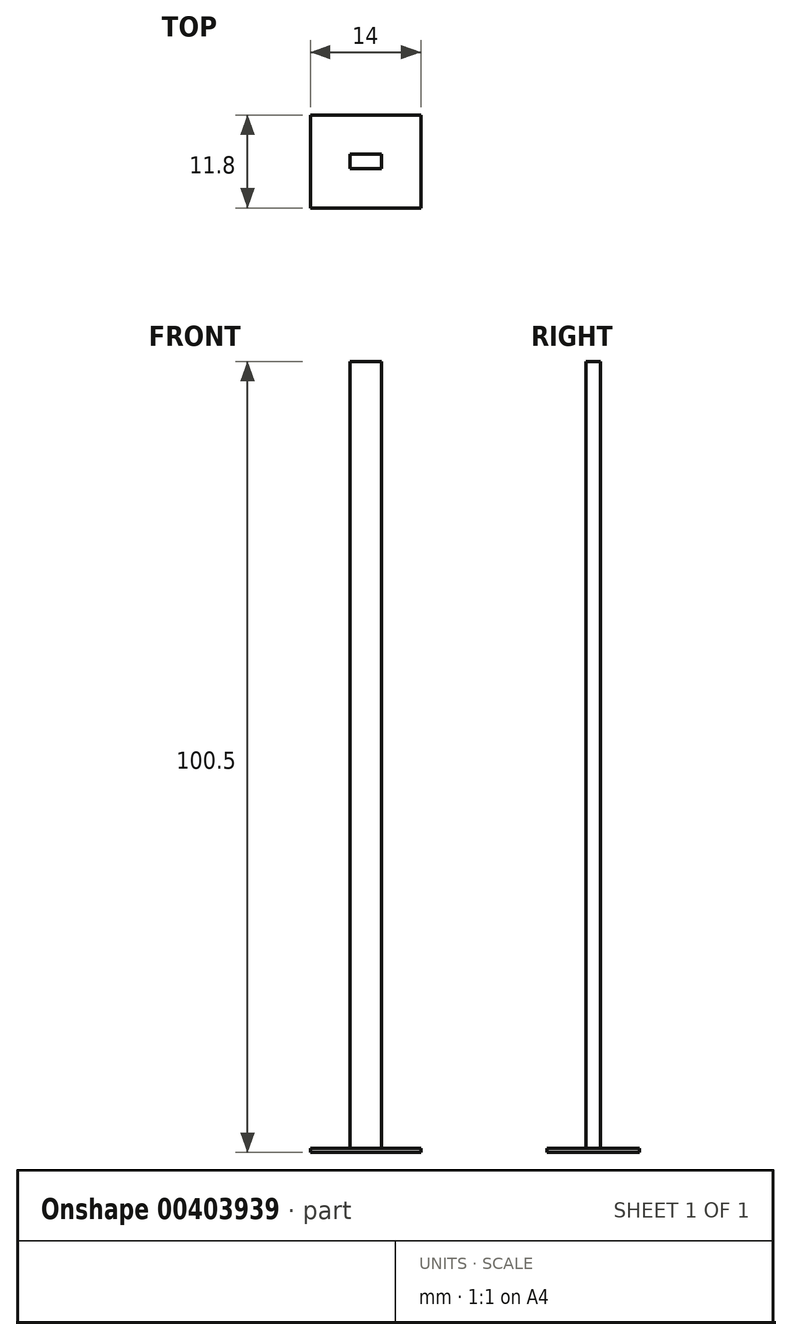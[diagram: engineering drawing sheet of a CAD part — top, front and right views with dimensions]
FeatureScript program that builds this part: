
annotation { "Feature Type Name" : "Feature", "Feature Type Description" : "" }
export const myFeature = defineFeature(function(context is Context, id is Id, definition is map)
    precondition{}
    {
        {
            var Q0;
            Q0=qCreatedBy(makeId("Top.planeOp"),FACE);
            var sketch = newSketch(context, id + "F0", { "sketchPlane" : qUnion([Q0])});
            skLineSegment(sketch, "E0.bottom", {"start": v(0, 0) * mm, "end": v(4, 0) * mm});
            skLineSegment(sketch, "E0.top", {"start": v(0, -1.8) * mm, "end": v(4, -1.8) * mm});
            skLineSegment(sketch, "E0.left", {"start": v(0, 0) * mm, "end": v(0, -1.8) * mm});
            skLineSegment(sketch, "E0.right", {"start": v(4, 0) * mm, "end": v(4, -1.8) * mm});
            skLineSegment(sketch, "E1.0", {"start": v(-5, 5) * mm, "end": v(9, 5) * mm});
            skLineSegment(sketch, "E1.1", {"start": v(-5, 5) * mm, "end": v(-5, -6.8) * mm});
            skLineSegment(sketch, "E1.2", {"start": v(-5, -6.8) * mm, "end": v(9, -6.8) * mm});
            skLineSegment(sketch, "E1.3", {"start": v(9, 5) * mm, "end": v(9, -6.8) * mm});
            skSolve(sketch);
        }
        {
            var Q0;
            Q0=makeQuery(id+"F0.imprint","IMPRINT",FACE,{"disambiguationData":[TD([[makeQuery(id+"F0.imprint","IMPRINT",EDGE,{"derivedFrom":sQuery(id+"F0.wireOp",EDGE,"E0.bottom")}),-1.0]])]});
            extrude(context, id + "F1", {"entities" : qUnion([Q0]), "depth" : 100 * mm});
        }
        {
            var Q0;
            Q0=makeQuery(id+"F0.imprint","IMPRINT",FACE,{"disambiguationData":[TD([[makeQuery(id+"F0.imprint","IMPRINT",EDGE,{"derivedFrom":sQuery(id+"F0.wireOp",EDGE,"E0.bottom")}),1.0]])]});
            var Q1;
            Q1=makeQuery(id+"F0.imprint","IMPRINT",FACE,{"disambiguationData":[TD([[makeQuery(id+"F0.imprint","IMPRINT",EDGE,{"derivedFrom":sQuery(id+"F0.wireOp",EDGE,"E0.bottom")}),-1.0]])]});
            extrude(context, id + "F2", {"entities" : qUnion([Q0, Q1]), "operationType" : NewBodyOperationType.ADD, "oppositeDirection" : true, "depth" : .5 * mm});
        }
    });
